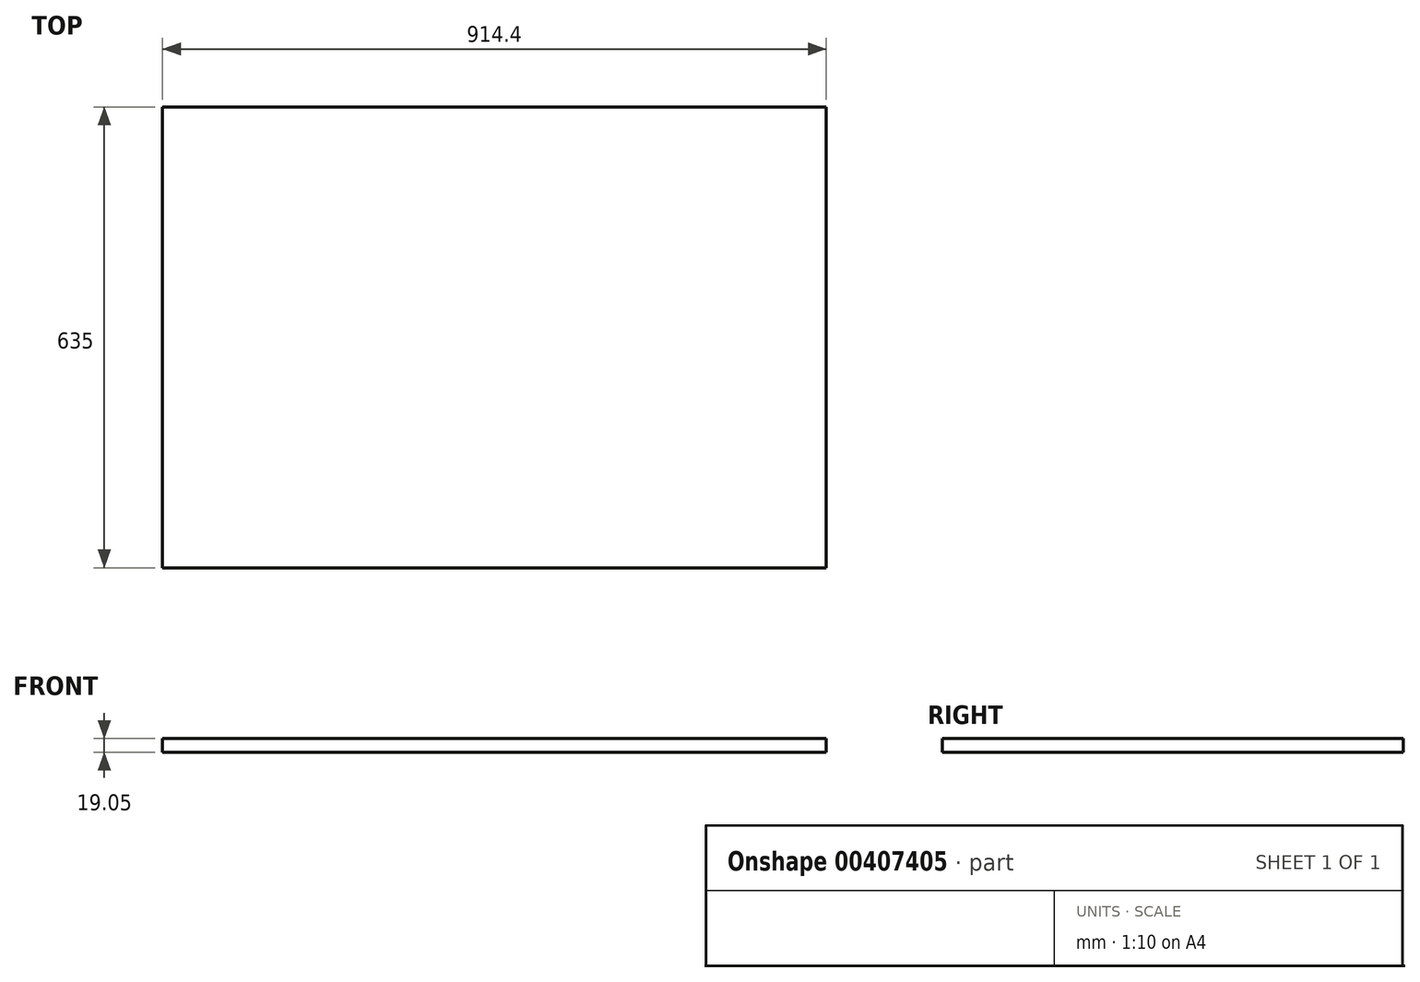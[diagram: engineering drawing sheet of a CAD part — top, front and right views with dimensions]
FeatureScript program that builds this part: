
annotation { "Feature Type Name" : "Feature", "Feature Type Description" : "" }
export const myFeature = defineFeature(function(context is Context, id is Id, definition is map)
    precondition{}
    {
        {
            var Q0;
            Q0=qCreatedBy(makeId("Top.planeOp"),FACE);
            var sketch = newSketch(context, id + "F0", { "sketchPlane" : qUnion([Q0])});
            skLineSegment(sketch, "E0.bottom", {"start": v(457.2, 317.5) * mm, "end": v(-457.2, 317.5) * mm});
            skLineSegment(sketch, "E0.top", {"start": v(457.2, -317.5) * mm, "end": v(-457.2, -317.5) * mm});
            skLineSegment(sketch, "E0.left", {"start": v(457.2, 317.5) * mm, "end": v(457.2, -317.5) * mm});
            skLineSegment(sketch, "E0.right", {"start": v(-457.2, 317.5) * mm, "end": v(-457.2, -317.5) * mm});
            skPoint(sketch, "E0.middle", {"position": v(0, 0) * mm});
            skSolve(sketch);
        }
        {
            var Q0;
            Q0=makeQuery(id+"F0.imprint","IMPRINT",FACE,{"disambiguationData":[TD([[makeQuery(id+"F0.imprint","IMPRINT",EDGE,{"derivedFrom":sQuery(id+"F0.wireOp",EDGE,"E0.bottom")}),1.0]])]});
            extrude(context, id + "F1", {"entities" : qUnion([Q0]), "depth" : 19.05 * mm});
        }
    });
